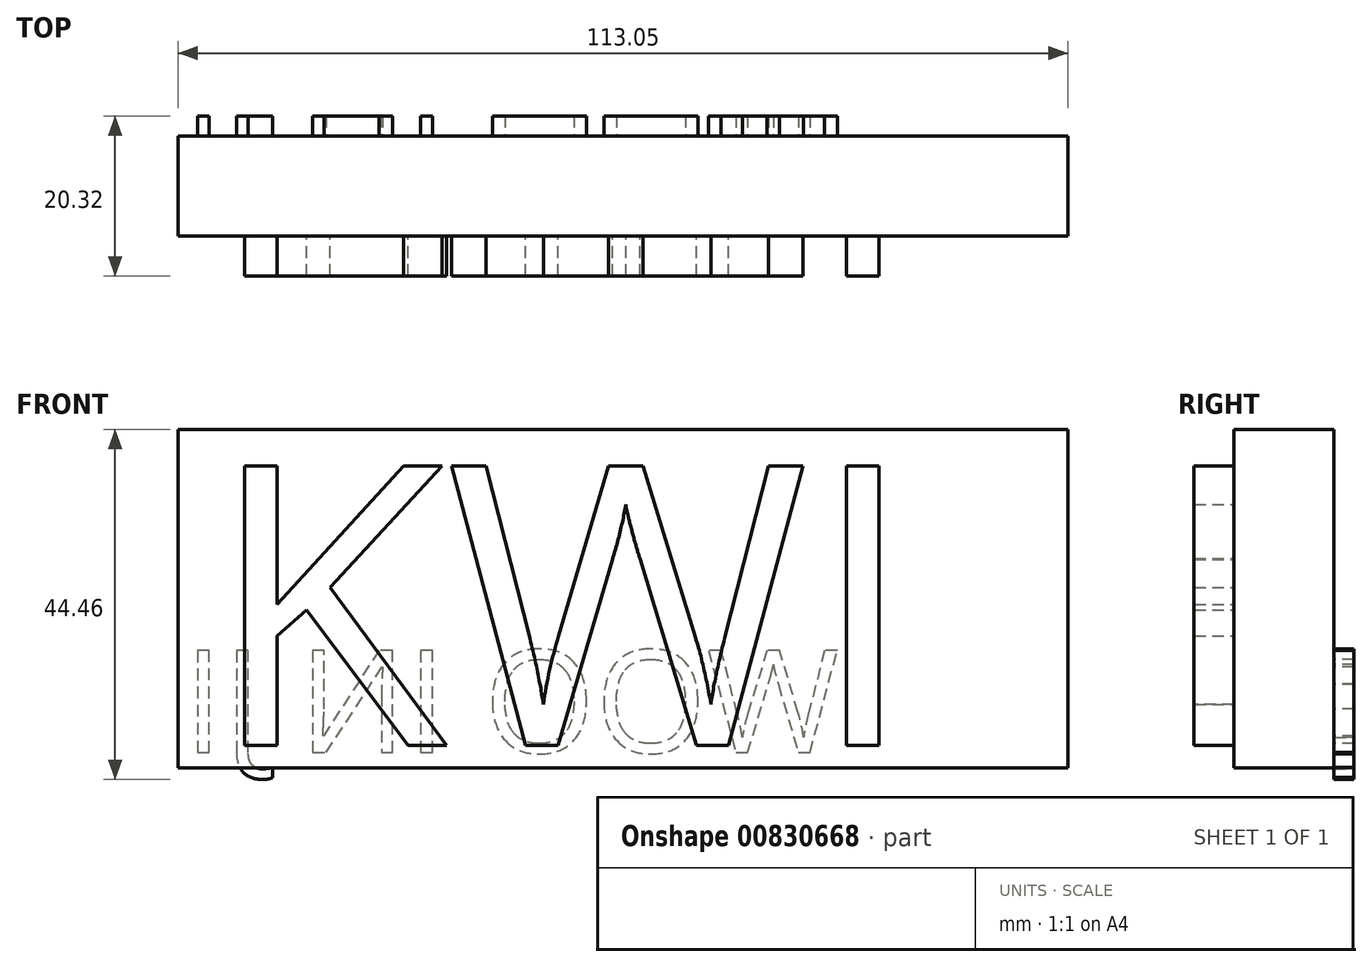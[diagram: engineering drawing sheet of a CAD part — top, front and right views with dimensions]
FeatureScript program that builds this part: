
annotation { "Feature Type Name" : "Feature", "Feature Type Description" : "" }
export const myFeature = defineFeature(function(context is Context, id is Id, definition is map)
    precondition{}
    {
        {
            var Q0;
            Q0=qCreatedBy(makeId("Front.planeOp"),FACE);
            var sketch = newSketch(context, id + "F0", { "sketchPlane" : qUnion([Q0])});
            skLineSegment(sketch, "E0.bottom", {"start": v(0, 0) * mm, "end": v(113.05, 0) * mm});
            skLineSegment(sketch, "E0.top", {"start": v(0, 42.98) * mm, "end": v(113.05, 42.98) * mm});
            skLineSegment(sketch, "E0.left", {"start": v(0, 0) * mm, "end": v(0, 42.98) * mm});
            skLineSegment(sketch, "E0.right", {"start": v(113.05, 0) * mm, "end": v(113.05, 42.98) * mm});
            skSolve(sketch);
        }
        {
            var Q0;
            Q0 = qSketchRegion(id + "F0", true);
            extrude(context, id + "F1", {"entities" : qUnion([Q0]), "depth" : 12.7 * mm, "offsetDistance" : 25.4 * mm});
        }
        {
            var Q0;
            Q0=makeQuery(id+"F1.opExtrude","CAP_FACE",FACE,{"disambiguationData":[OSD([sQuery(id+"F0.wireOp",EDGE,"E0.bottom"),sQuery(id+"F0.wireOp",EDGE,"E0.top"),sQuery(id+"F0.wireOp",EDGE,"E0.left"),sQuery(id+"F0.wireOp",EDGE,"E0.right")])],"isStart":false});
            var sketch = newSketch(context, id + "F2", { "sketchPlane" : qUnion([Q0])});
            skText(sketch, "E1", { "text": "KWI", "fontName": "OpenSans-Regular.ttf"});
            const initialGuessF2  = {"E1": [0.00358, 0.00286, 1, 0, 0.03576]};
            skSetInitialGuess(sketch, initialGuessF2);
            skSolve(sketch);
        }
        {
            var Q0;
            Q0 = qSketchRegion(id + "F2", true);
            extrude(context, id + "F3", {"entities" : qUnion([Q0]), "operationType" : NewBodyOperationType.ADD, "depth" : 5.08 * mm, "offsetDistance" : 25.4 * mm});
        }
        {
            var Q0;
            Q0=makeQuery(id+"F1.opExtrude","CAP_FACE",FACE,{"disambiguationData":[OSD([sQuery(id+"F0.wireOp",EDGE,"E0.bottom"),sQuery(id+"F0.wireOp",EDGE,"E0.top"),sQuery(id+"F0.wireOp",EDGE,"E0.left"),sQuery(id+"F0.wireOp",EDGE,"E0.right")])],"isStart":true});
            var sketch = newSketch(context, id + "F4", { "sketchPlane" : qUnion([Q0])});
            skText(sketch, "E2", { "text": "WOO IN JI", "fontName": "OpenSans-Regular.ttf"});
            const initialGuessF4  = {"E2": [-0.08396, 0.00194, 1, 0, 0.01309]};
            skSetInitialGuess(sketch, initialGuessF4);
            skSolve(sketch);
        }
        {
            var Q0;
            Q0 = qSketchRegion(id + "F4", true);
            extrude(context, id + "F5", {"entities" : qUnion([Q0]), "operationType" : NewBodyOperationType.ADD, "depth" : 2.54 * mm, "offsetDistance" : 25.4 * mm});
        }
    });
